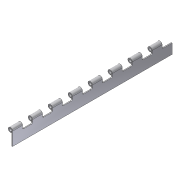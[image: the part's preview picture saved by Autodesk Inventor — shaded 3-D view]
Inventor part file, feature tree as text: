
AUTODESK INVENTOR PART (.ipt)
format: ipt  version: 2012 (Build 160160000, 160)  size: 142,848 bytes
history: native  units: in
note: dims shown in document units (in); Inventor stores cm internally (conversion verified against a paired STEP export)
features: extrude x2, sketch x2, fillet x1, pattern_linear x1, projected_geometry x1
ambient origin geometry x8: Origin, YZ Plane, XZ Plane, XY Plane, X Axis, Y Axis, Z Axis, Center Point
bodies: Solid1 (feature_tree)
feature tree (7):
  extrude  "Extrusion1"  Depth=0.09in
  extrude  "Extrusion2"  Depth=16.0in TaperAngle=0.0deg
  fillet  "Fillet1"  Radius=1.0in
  pattern_linear  "Rectangular Pattern1"  Spacing1=1.0in  [1 undecoded]
  sketch  "Sketch1"  dims[d0=0.445in d1=0.09in]
  sketch  "Sketch2"  dims[d2=0.09in d3=16.0in d4=0.0in d5=1.0in d6=1.0in d7=0.125in d8=16.0in d9=0.0in d10=0.125in d11=3.1496in d13=2.0in]
  projected_geometry  "Projected Loop1"
note: 1 required parameter value undecoded (feature->parameter linkage not recoverable at this tier; creation-order binding heuristic only, values carry confidence <= 0.55)
